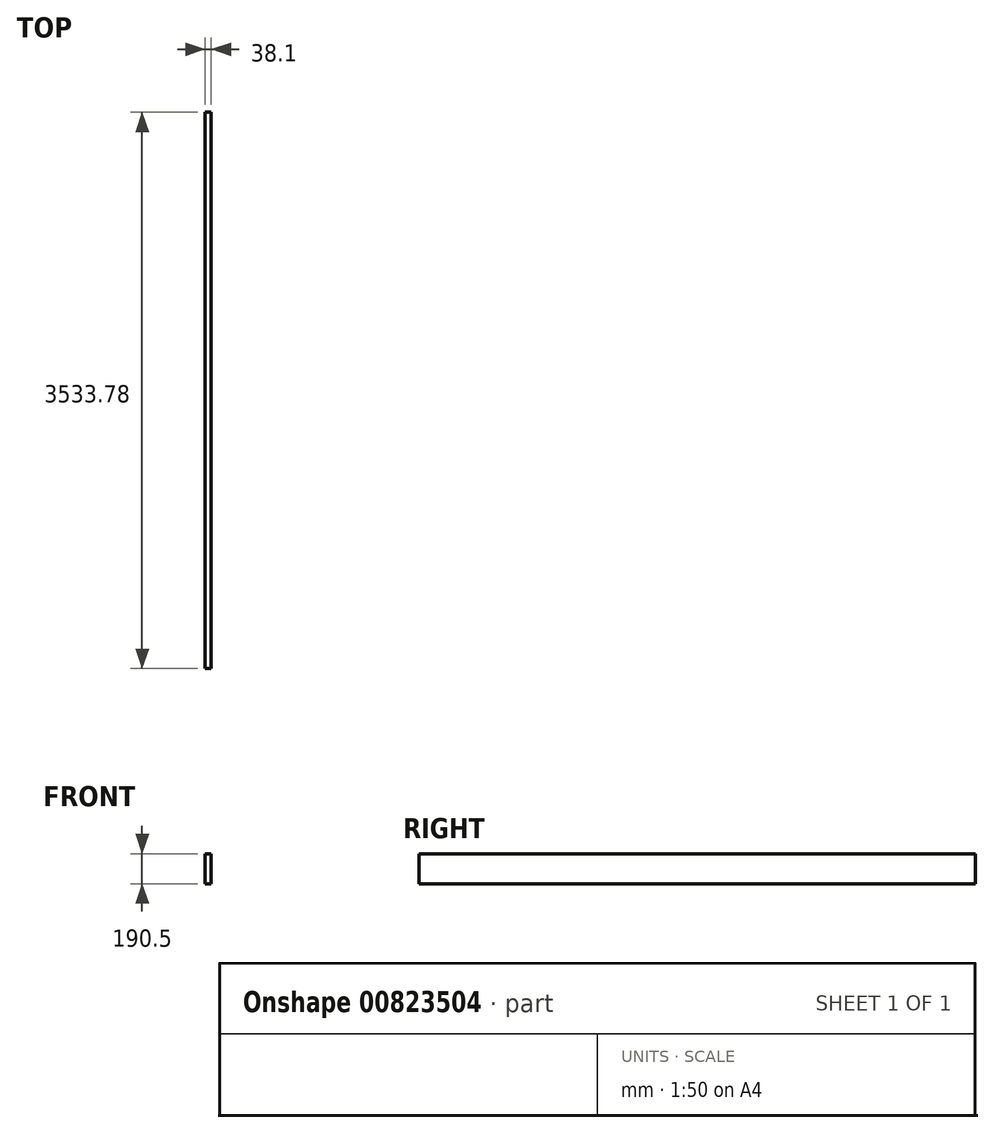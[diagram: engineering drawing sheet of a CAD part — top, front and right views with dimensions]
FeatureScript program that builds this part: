
annotation { "Feature Type Name" : "Feature", "Feature Type Description" : "" }
export const myFeature = defineFeature(function(context is Context, id is Id, definition is map)
    precondition{}
    {
        {
            var Q0;
            Q0=qCreatedBy(makeId("Front.planeOp"),FACE);
            var sketch = newSketch(context, id + "F0", { "sketchPlane" : qUnion([Q0])});
            skLineSegment(sketch, "E0.bottom", {"start": v(0, 0) * mm, "end": v(38.1, 0) * mm});
            skLineSegment(sketch, "E0.top", {"start": v(0, 190.5) * mm, "end": v(38.1, 190.5) * mm});
            skLineSegment(sketch, "E0.left", {"start": v(0, 0) * mm, "end": v(0, 190.5) * mm});
            skLineSegment(sketch, "E0.right", {"start": v(38.1, 0) * mm, "end": v(38.1, 190.5) * mm});
            skSolve(sketch);
        }
        {
            var Q0;
            Q0=qSketchRegion(id+"F0",true);
            extrude(context, id + "F1", {"entities" : qUnion([Q0]), "depth" : 3533.77 * mm, "offsetDistance" : 25.4 * mm});
        }
    });
